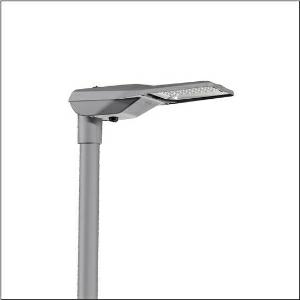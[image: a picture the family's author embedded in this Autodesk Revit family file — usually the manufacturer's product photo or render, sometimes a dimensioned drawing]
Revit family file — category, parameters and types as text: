
# Revit family: streetlight_sl_21_iq_mini___p1_0a_5xe2a31y08hb_fafd
name_source: partatom
category: Lighting Fixtures
units: mm (PartAtom-declared; Revit-internal decimal feet)

## family parameters
Cut with Voids When Loaded = No
Host = Face
Light Source = No
Part Type = Normal
Room Calculation Point = No
Round Connector Dimension = Use Diameter
Shared = No

## types (1)
- --- (1 x LED, 9750 lm, 71 W, 3000K)
    Apparent Load = 71 VA
    CIE Flux Codes = 21 50 90 100 100
    Color Rendering = 70
    Color Temperature = 3000K
    Default Elevation = 1800 mm
    Description = Streetlight SL 21 iQ mini, mast luminaire, primary light control with lens, of PMMA, primary optical cover: cover, of toughened safety glass, transparent, light distribution: P1.0a, light emission: direct distribution, primary light characteristic: asymmetric, installation type: post-top, side-entry, LED, High Power LED, rated luminous flux: 9.750lm, luminous efficacy: 137lm/W, light colour: 730, colour temperature: 3000K, control gear: iQ-Street Remote, D4i with power reduction, control: pre-setting: logarithmic dimming characteristic, Street-Remote, Auto-Match, Temp-Guard, Lumen-Switch, Night-Set, Smart-Wire, Light-Fading, Desk-Remote (wireless, voltage-free reading and setting of iQ features in the workshop via application-optimized NFC function/RFID function), optimised constant luminous flux control (CLO 2.0), mains connection: 220..240V, AC, 50/60Hz, start of lifetime: 71W, end of service life: 75W, reduction: 30W, luminaire housing, of diecast aluminium, powder-coated, SITECO metallic grey (DB 702S), corrosivity category C5 high according to DIN EN ISO 12944, please order mast flange separately, inclination adjustable: 0°, 5°, 10°, 15°, sealing non-destructively replaceable, multi-level sealing system, length: 628mm, width: 235mm, height: 110mm, mast flange for spigot size: 42mm (side-entry): 5XC10008XM4, 60/48mm (side-entry/post-top): 5XC10108XM2, 76/60mm (side-entry/post-top): 5XC10108XM1, mounting height: 4..8m, Smart Interface below and above, protection rating (complete): IP66, insulation class (complete): insulation class II (safety insulation), certification: CE, ENEC, ENEC+, VDE, impact resistance: IK10, permissible operating ambient temperature for outdoor applications: -40..+50°C, standard-compliant lighting for roads and squares, packaging unit: 1 piece

Light Distribution: P1.0a
    Height = 110 mm
    Lamp = 1 x LED
    Lamp Light Flux = 9750 lm
    Lamp Power = 71 W
    Lamp count = 1
    Length = 625 mm
    Luminous efficacy = 137 lm/W
    Manufacturer = Siteco
    ModVariant = No
    Model = 5XE2A31Y08HB
    Number of Poles = 1
    OnlyDefault = Yes
    Power Factor = 1
    Product Name = Streetlight SL 21 iQ mini | P1.0a
    Product group = mast luminaire | pylon top
    ProductGroupID = 6100
    Protection Class = Protection class II
    Protection Degree = IP 66
    RLX_Detail_Level = 1
    RLX_Emergency_Light_Flux = 0 lm
    RLX_Emergency_Type = 0
    RLX_Emergency_Type_DB = No
    RlxData = <blob elided: 103933 chars, md5=7d006ed8>
    Socket = socket
    Standby Power = 0 W
    System Light Flux = 9750 lm
    System Power = 71 W
    Type Comments = factory setting: luminous flux: 100 % | dim-lin: 254 | 716 mA
    Type Image = l_1003514.jpg
    URL = http://relux.com
    VarID = @adj_113623
    Voltage = 0 V
    Weight = 0.00 kg
    Width = 234 mm

## geometry (parser evidence)
native form markers: Blend x4, Sweep x10
no freeform markers — native parametric forms only
